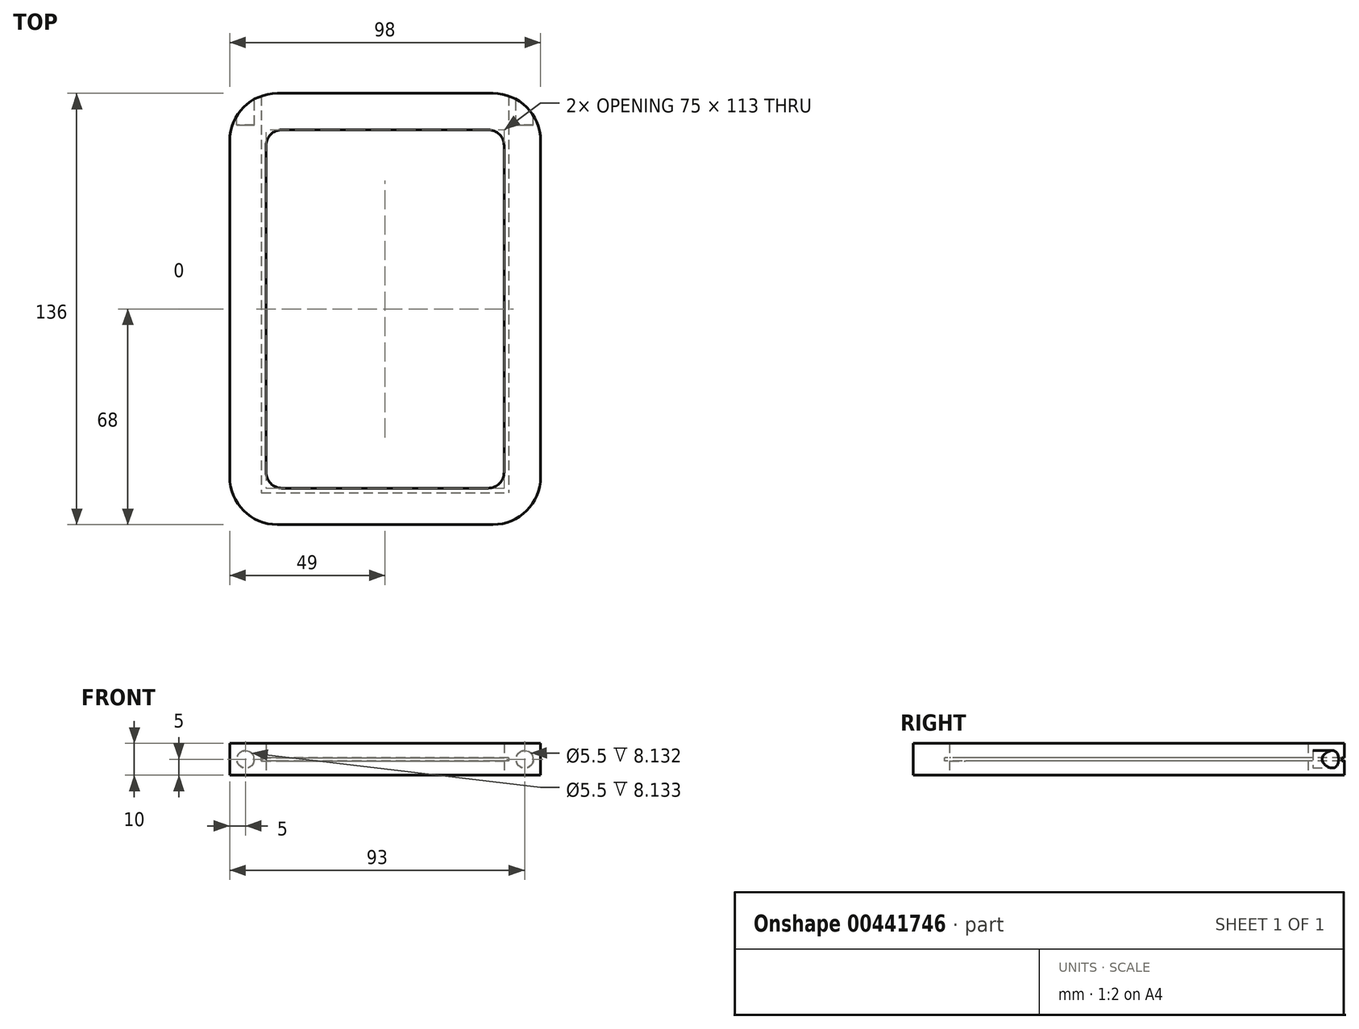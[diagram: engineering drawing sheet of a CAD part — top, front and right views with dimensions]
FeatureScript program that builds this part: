
annotation { "Feature Type Name" : "Feature", "Feature Type Description" : "" }
export const myFeature = defineFeature(function(context is Context, id is Id, definition is map)
    precondition{}
    {
        {
            var Q0;
            Q0=qCreatedBy(makeId("Top.planeOp"),FACE);
            var sketch = newSketch(context, id + "F0", { "sketchPlane" : qUnion([Q0])});
            skLineSegment(sketch, "E0.bottom", {"start": v(-39, 58) * mm, "end": v(39, 58) * mm});
            skLineSegment(sketch, "E0.top", {"start": v(-39, -58) * mm, "end": v(39, -58) * mm});
            skLineSegment(sketch, "E0.left", {"start": v(-39, 58) * mm, "end": v(-39, -58) * mm});
            skLineSegment(sketch, "E0.right", {"start": v(39, 58) * mm, "end": v(39, -58) * mm});
            skPoint(sketch, "E0.middle", {"position": v(0, 0) * mm});
            skLineSegment(sketch, "E1.bottom", {"start": v(-37.5, 56.5) * mm, "end": v(37.5, 56.5) * mm});
            skLineSegment(sketch, "E1.top", {"start": v(-37.5, -56.5) * mm, "end": v(37.5, -56.5) * mm});
            skLineSegment(sketch, "E1.left", {"start": v(-37.5, 56.5) * mm, "end": v(-37.5, -56.5) * mm});
            skLineSegment(sketch, "E1.right", {"start": v(37.5, 56.5) * mm, "end": v(37.5, -56.5) * mm});
            skLineSegment(sketch, "E2.bottom", {"start": v(49, -68) * mm, "end": v(-49, -68) * mm});
            skLineSegment(sketch, "E2.top", {"start": v(49, 68) * mm, "end": v(-49, 68) * mm});
            skLineSegment(sketch, "E2.left", {"start": v(49, -68) * mm, "end": v(49, 68) * mm});
            skLineSegment(sketch, "E2.right", {"start": v(-49, -68) * mm, "end": v(-49, 68) * mm});
            skSolve(sketch);
        }
        {
            var Q0;
            Q0=makeQuery(id+"F0.imprint","IMPRINT",FACE,{"disambiguationData":[TD([[makeQuery(id+"F0.imprint","IMPRINT",EDGE,{"derivedFrom":sQuery(id+"F0.wireOp",EDGE,"E0.bottom")}),-1.0]])]});
            var Q1;
            Q1=makeQuery(id+"F0.imprint","IMPRINT",FACE,{"disambiguationData":[TD([[makeQuery(id+"F0.imprint","IMPRINT",EDGE,{"derivedFrom":sQuery(id+"F0.wireOp",EDGE,"E0.bottom")}),1.0]])]});
            extrude(context, id + "F1", {"entities" : qUnion([Q0, Q1]), "endBound" : BoundingType.SYMMETRIC, "depth" : 10 * mm});
        }
        {
            var Q0;
            Q0=qCreatedBy(makeId("Top.planeOp"),FACE);
            var sketch = newSketch(context, id + "F2", { "sketchPlane" : qUnion([Q0])});
            skLineSegment(sketch, "E3.bottom", {"start": v(-39, 72) * mm, "end": v(39, 72) * mm});
            skLineSegment(sketch, "E3.top", {"start": v(-39, -58) * mm, "end": v(39, -58) * mm});
            skLineSegment(sketch, "E3.left", {"start": v(-39, 72) * mm, "end": v(-39, -58) * mm});
            skLineSegment(sketch, "E3.right", {"start": v(39, 72) * mm, "end": v(39, -58) * mm});
            skPoint(sketch, "E3.middle", {"position": v(0, 7) * mm});
            skSolve(sketch);
        }
        {
            var Q0;
            Q0 = qSketchRegion(id + "F2", true);
            extrude(context, id + "F3", {"entities" : qUnion([Q0]), "operationType" : NewBodyOperationType.REMOVE, "endBound" : BoundingType.SYMMETRIC, "oppositeDirection" : true, "depth" : 1 * mm});
        }
        {
            var Q0;
            Q0=makeQuery(id+"F1.opExtrude","SWEPT_FACE",FACE,{"disambiguationData":[OSD([sQuery(id+"F0.wireOp",EDGE,"E2.top")])]});
            var sketch = newSketch(context, id + "F4", { "sketchPlane" : qUnion([Q0])});
            skCircle(sketch, "E4", {"center": v(44, 0) * mm, "radius": 2.75 * mm});
            skCircle(sketch, "E5", {"center": v(-44, 0) * mm, "radius": 2.75 * mm});
            skSolve(sketch);
        }
        {
            var Q0;
            Q0=makeQuery(id+"F1.opExtrude","SWEPT_EDGE",EDGE,{"disambiguationData":[OSD([sQuery(id+"F0.wireOp",EDGE,"E2.bottom"),sQuery(id+"F0.wireOp",EDGE,"E2.right")])]});
            var Q1;
            Q1=makeQuery(id+"F1.opExtrude","SWEPT_EDGE",EDGE,{"disambiguationData":[OSD([sQuery(id+"F0.wireOp",EDGE,"E2.bottom"),sQuery(id+"F0.wireOp",EDGE,"E2.left")])]});
            var Q2;
            Q2=makeQuery(id+"F1.opExtrude","SWEPT_EDGE",EDGE,{"disambiguationData":[OSD([sQuery(id+"F0.wireOp",EDGE,"E2.top"),sQuery(id+"F0.wireOp",EDGE,"E2.left")])]});
            var Q3;
            Q3=makeQuery(id+"F1.opExtrude","SWEPT_EDGE",EDGE,{"disambiguationData":[OSD([sQuery(id+"F0.wireOp",EDGE,"E2.top"),sQuery(id+"F0.wireOp",EDGE,"E2.right")])]});
            fillet(context, id + "F5", {"entities" : qUnion([Q0, Q1, Q2, Q3]), "radius" : 15 * mm, "tangentPropagation" : true, "allowEdgeOverflow" : false});
        }
        {
            var Q0;
            {var subQ0=sQuery(id+"F0.wireOp",EDGE,"E1.right");var subQ1=sQuery(id+"F0.wireOp",EDGE,"E1.top");Q0=makeQuery(id+"F3.boolean.opBoolean","SPLIT",EDGE,{"disambiguationData":[TD([makeQuery(id+"F3.opExtrude","CAP_FACE",FACE,{"disambiguationData":[OSD([sQuery(id+"F2.wireOp",EDGE,"E3.bottom"),sQuery(id+"F2.wireOp",EDGE,"E3.top"),sQuery(id+"F2.wireOp",EDGE,"E3.left"),sQuery(id+"F2.wireOp",EDGE,"E3.right")])],"isStart":false})])],"derivedFrom":makeQuery(id+"F1.opExtrude","SWEPT_EDGE",EDGE,{"disambiguationData":[OSD([subQ1,subQ0])]})});}
            var Q1;
            {var subQ0=sQuery(id+"F0.wireOp",EDGE,"E1.right");var subQ1=sQuery(id+"F0.wireOp",EDGE,"E1.top");Q1=makeQuery(id+"F3.boolean.opBoolean","SPLIT",EDGE,{"disambiguationData":[TD([makeQuery(id+"F3.opExtrude","CAP_FACE",FACE,{"disambiguationData":[OSD([sQuery(id+"F2.wireOp",EDGE,"E3.bottom"),sQuery(id+"F2.wireOp",EDGE,"E3.top"),sQuery(id+"F2.wireOp",EDGE,"E3.left"),sQuery(id+"F2.wireOp",EDGE,"E3.right")])],"isStart":true})])],"derivedFrom":makeQuery(id+"F1.opExtrude","SWEPT_EDGE",EDGE,{"disambiguationData":[OSD([subQ1,subQ0])]})});}
            var Q2;
            {var subQ0=sQuery(id+"F0.wireOp",EDGE,"E1.left");var subQ1=sQuery(id+"F0.wireOp",EDGE,"E1.top");Q2=makeQuery(id+"F3.boolean.opBoolean","SPLIT",EDGE,{"disambiguationData":[TD([makeQuery(id+"F3.opExtrude","CAP_FACE",FACE,{"disambiguationData":[OSD([sQuery(id+"F2.wireOp",EDGE,"E3.bottom"),sQuery(id+"F2.wireOp",EDGE,"E3.top"),sQuery(id+"F2.wireOp",EDGE,"E3.left"),sQuery(id+"F2.wireOp",EDGE,"E3.right")])],"isStart":true})])],"derivedFrom":makeQuery(id+"F1.opExtrude","SWEPT_EDGE",EDGE,{"disambiguationData":[OSD([subQ1,subQ0])]})});}
            var Q3;
            {var subQ0=sQuery(id+"F0.wireOp",EDGE,"E1.left");var subQ1=sQuery(id+"F0.wireOp",EDGE,"E1.top");Q3=makeQuery(id+"F3.boolean.opBoolean","SPLIT",EDGE,{"disambiguationData":[TD([makeQuery(id+"F3.opExtrude","CAP_FACE",FACE,{"disambiguationData":[OSD([sQuery(id+"F2.wireOp",EDGE,"E3.bottom"),sQuery(id+"F2.wireOp",EDGE,"E3.top"),sQuery(id+"F2.wireOp",EDGE,"E3.left"),sQuery(id+"F2.wireOp",EDGE,"E3.right")])],"isStart":false})])],"derivedFrom":makeQuery(id+"F1.opExtrude","SWEPT_EDGE",EDGE,{"disambiguationData":[OSD([subQ1,subQ0])]})});}
            var Q4;
            {var subQ0=sQuery(id+"F0.wireOp",EDGE,"E1.bottom");var subQ1=sQuery(id+"F0.wireOp",EDGE,"E1.left");Q4=makeQuery(id+"F3.boolean.opBoolean","SPLIT",EDGE,{"disambiguationData":[TD([makeQuery(id+"F3.opExtrude","CAP_FACE",FACE,{"disambiguationData":[OSD([sQuery(id+"F2.wireOp",EDGE,"E3.bottom"),sQuery(id+"F2.wireOp",EDGE,"E3.top"),sQuery(id+"F2.wireOp",EDGE,"E3.left"),sQuery(id+"F2.wireOp",EDGE,"E3.right")])],"isStart":true})])],"derivedFrom":makeQuery(id+"F1.opExtrude","SWEPT_EDGE",EDGE,{"disambiguationData":[OSD([subQ0,subQ1])]})});}
            var Q5;
            {var subQ0=sQuery(id+"F0.wireOp",EDGE,"E1.bottom");var subQ1=sQuery(id+"F0.wireOp",EDGE,"E1.left");Q5=makeQuery(id+"F3.boolean.opBoolean","SPLIT",EDGE,{"disambiguationData":[TD([makeQuery(id+"F3.opExtrude","CAP_FACE",FACE,{"disambiguationData":[OSD([sQuery(id+"F2.wireOp",EDGE,"E3.bottom"),sQuery(id+"F2.wireOp",EDGE,"E3.top"),sQuery(id+"F2.wireOp",EDGE,"E3.left"),sQuery(id+"F2.wireOp",EDGE,"E3.right")])],"isStart":false})])],"derivedFrom":makeQuery(id+"F1.opExtrude","SWEPT_EDGE",EDGE,{"disambiguationData":[OSD([subQ0,subQ1])]})});}
            var Q6;
            {var subQ0=sQuery(id+"F0.wireOp",EDGE,"E1.bottom");var subQ1=sQuery(id+"F0.wireOp",EDGE,"E1.right");Q6=makeQuery(id+"F3.boolean.opBoolean","SPLIT",EDGE,{"disambiguationData":[TD([makeQuery(id+"F3.opExtrude","CAP_FACE",FACE,{"disambiguationData":[OSD([sQuery(id+"F2.wireOp",EDGE,"E3.bottom"),sQuery(id+"F2.wireOp",EDGE,"E3.top"),sQuery(id+"F2.wireOp",EDGE,"E3.left"),sQuery(id+"F2.wireOp",EDGE,"E3.right")])],"isStart":false})])],"derivedFrom":makeQuery(id+"F1.opExtrude","SWEPT_EDGE",EDGE,{"disambiguationData":[OSD([subQ0,subQ1])]})});}
            var Q7;
            {var subQ0=sQuery(id+"F0.wireOp",EDGE,"E1.bottom");var subQ1=sQuery(id+"F0.wireOp",EDGE,"E1.right");Q7=makeQuery(id+"F3.boolean.opBoolean","SPLIT",EDGE,{"disambiguationData":[TD([makeQuery(id+"F3.opExtrude","CAP_FACE",FACE,{"disambiguationData":[OSD([sQuery(id+"F2.wireOp",EDGE,"E3.bottom"),sQuery(id+"F2.wireOp",EDGE,"E3.top"),sQuery(id+"F2.wireOp",EDGE,"E3.left"),sQuery(id+"F2.wireOp",EDGE,"E3.right")])],"isStart":true})])],"derivedFrom":makeQuery(id+"F1.opExtrude","SWEPT_EDGE",EDGE,{"disambiguationData":[OSD([subQ0,subQ1])]})});}
            fillet(context, id + "F6", {"entities" : qUnion([Q0, Q1, Q2, Q3, Q4, Q5, Q6, Q7]), "radius" : 5 * mm, "tangentPropagation" : true, "allowEdgeOverflow" : false});
        }
        {
            var Q0;
            Q0=makeQuery(id+"F4.imprint","IMPRINT",FACE,{"disambiguationData":[TD([[makeQuery(id+"F4.imprint","IMPRINT",EDGE,{"derivedFrom":sQuery(id+"F4.wireOp",EDGE,"E4")}),1.0]])]});
            var Q1;
            Q1=makeQuery(id+"F4.imprint","IMPRINT",FACE,{"disambiguationData":[TD([[makeQuery(id+"F4.imprint","IMPRINT",EDGE,{"derivedFrom":sQuery(id+"F4.wireOp",EDGE,"E5")}),1.0]])]});
            extrude(context, id + "F7", {"entities" : qUnion([Q0, Q1]), "operationType" : NewBodyOperationType.REMOVE, "oppositeDirection" : true, "depth" : 10 * mm});
        }
    });
